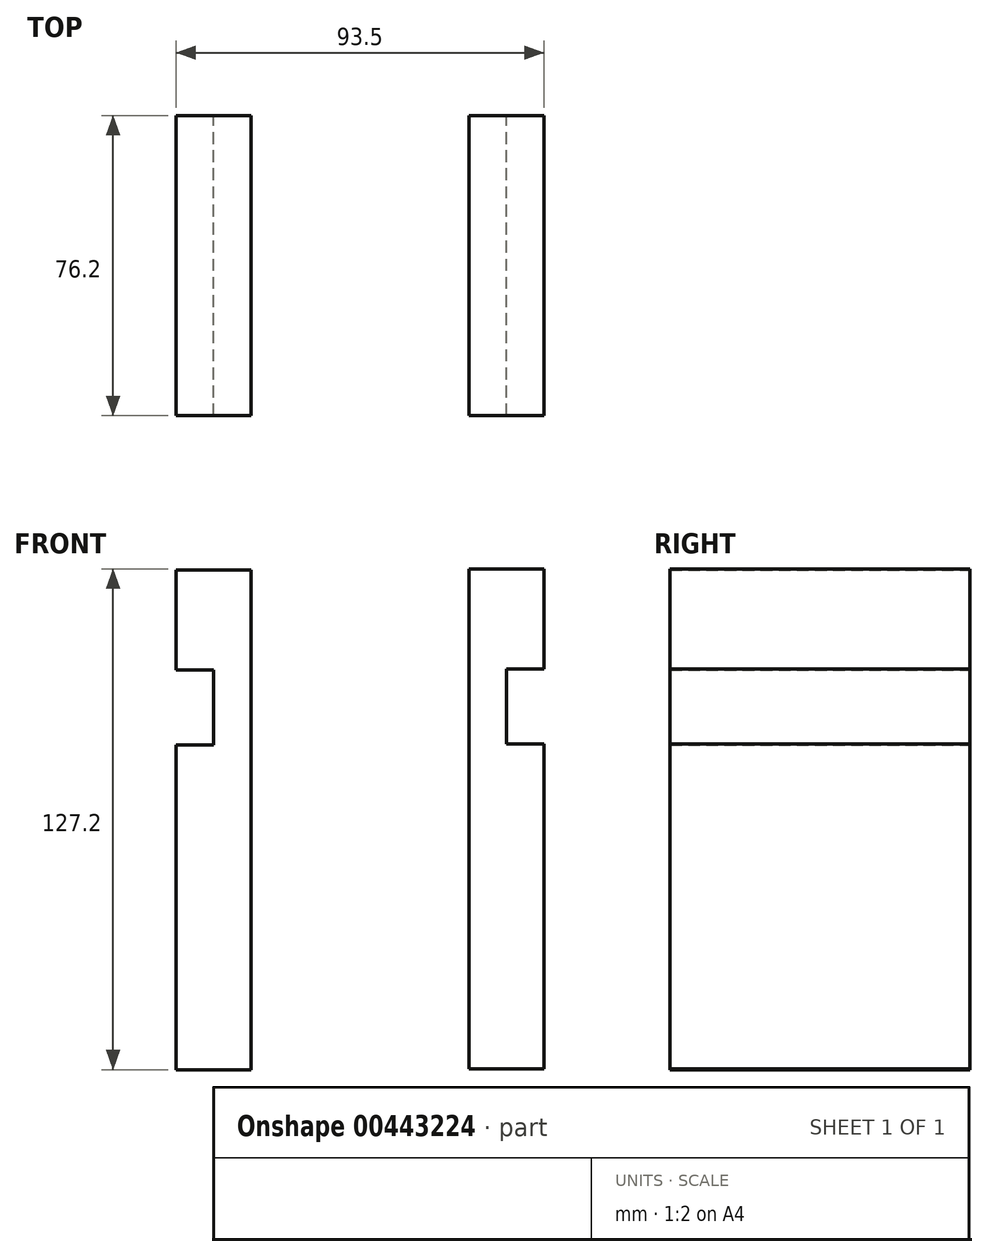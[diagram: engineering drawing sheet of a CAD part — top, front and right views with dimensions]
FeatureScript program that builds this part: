
annotation { "Feature Type Name" : "Feature", "Feature Type Description" : "" }
export const myFeature = defineFeature(function(context is Context, id is Id, definition is map)
    precondition{}
    {
        {
            var Q0;
            Q0=qCreatedBy(makeId("Front.planeOp"),FACE);
            var sketch = newSketch(context, id + "F0", { "sketchPlane" : qUnion([Q0])});
            skLineSegment(sketch, "E0", {"start": v(-56.92, -57.18) * mm, "end": v(-37.87, -57.18) * mm});
            skLineSegment(sketch, "E1", {"start": v(-37.87, -57.18) * mm, "end": v(-37.87, 69.82) * mm});
            skLineSegment(sketch, "E2", {"start": v(-37.87, 69.82) * mm, "end": v(-56.92, 69.82) * mm});
            skLineSegment(sketch, "E3", {"start": v(-56.92, 69.82) * mm, "end": v(-56.92, 44.42) * mm});
            skLineSegment(sketch, "E4", {"start": v(-56.92, 44.42) * mm, "end": v(-47.4, 44.42) * mm});
            skLineSegment(sketch, "E5", {"start": v(-47.4, 44.42) * mm, "end": v(-47.4, 25.37) * mm});
            skLineSegment(sketch, "E6", {"start": v(-47.4, 25.37) * mm, "end": v(-56.92, 25.37) * mm});
            skLineSegment(sketch, "E7", {"start": v(-56.92, 25.37) * mm, "end": v(-56.92, -57.18) * mm});
            skSolve(sketch);
        }
        {
            var Q0;
            Q0 = qSketchRegion(id + "F0", true);
            extrude(context, id + "F1", {"entities" : qUnion([Q0]), "depth" : 76.2 * mm});
        }
        {
            var Q0;
            Q0=qCreatedBy(makeId("Front.planeOp"),FACE);
            var sketch = newSketch(context, id + "F2", { "sketchPlane" : qUnion([Q0])});
            skLineSegment(sketch, "E8", {"start": v(36.58, -56.98) * mm, "end": v(17.53, -56.98) * mm});
            skLineSegment(sketch, "E9", {"start": v(17.53, -56.98) * mm, "end": v(17.53, 70.02) * mm});
            skLineSegment(sketch, "E10", {"start": v(17.53, 70.02) * mm, "end": v(36.58, 70.02) * mm});
            skLineSegment(sketch, "E11", {"start": v(36.58, 70.02) * mm, "end": v(36.58, 44.62) * mm});
            skLineSegment(sketch, "E12", {"start": v(36.58, 44.62) * mm, "end": v(27.06, 44.62) * mm});
            skLineSegment(sketch, "E13", {"start": v(27.06, 44.62) * mm, "end": v(27.06, 25.57) * mm});
            skLineSegment(sketch, "E14", {"start": v(27.06, 25.57) * mm, "end": v(36.58, 25.57) * mm});
            skLineSegment(sketch, "E15", {"start": v(36.58, 25.57) * mm, "end": v(36.58, -56.98) * mm});
            skSolve(sketch);
        }
        {
            var Q0;
            Q0 = qSketchRegion(id + "F2", true);
            extrude(context, id + "F3", {"entities" : qUnion([Q0]), "depth" : 76.2 * mm});
        }
    });
